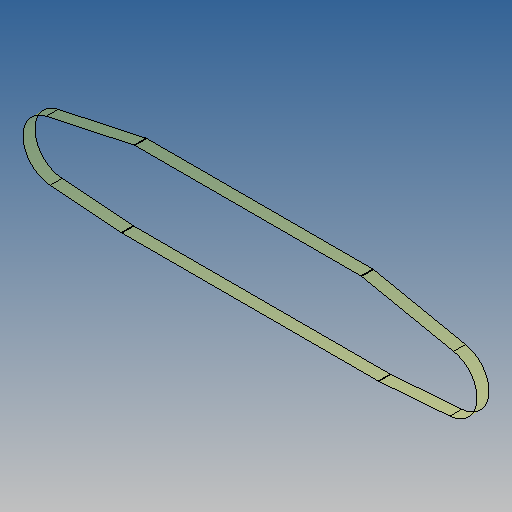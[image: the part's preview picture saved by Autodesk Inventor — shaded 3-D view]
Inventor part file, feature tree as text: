
AUTODESK INVENTOR PART (.ipt)
format: ipt  version: 2025 (Build 290162010, 162A)  size: 108,544 bytes
history: native  units: mm
features: sketch x1, other x1, extrude x1
ambient origin geometry x8: Origin, YZ Plane, XZ Plane, XY Plane, X Axis, Y Axis, Z Axis, Center Point
bodies: Body1 (feature_tree)
feature tree (3):
  sketch  "Skizze1"  dims[d0=53.928mm d1=364.0mm d2=31.9mm d3=24.0mm d4=64.0mm d5=64.0mm d6=40.0mm d7=76.0mm d8=80.0mm d9=3.9mm d17=11.0mm d18=0.0mm]
  other  "Flä1"
  extrude  "Extrusionsfläche1"  Depth=364.0mm
